# Revit family: VT.VAR10.G.07
name_source: partatom
category: Оборудование
units: mm (PartAtom-declared; Revit-internal decimal feet)

## family parameters
Всегда вертикально = Да
Заголовок OmniClass = Climate Control (HVAC)
На основе рабочей плоскости = Нет
Номер OmniClass = 23.75.00.00
Общий = Нет
При загрузке вырезать с полостями = Нет
Размер круглого соединителя = Использовать диаметр
Тип детали = Нормальный
Точка расчета площади = Нет

## types (1)
- VT.VAR10.G.07
    Article Type = VAR 10
    BIMобъект категории = Другие
    BIMобъект основная категория = Водопровод
    Produced in = Made in Italy
    Product certification = https://www.ivar-group.com
    Revit Version = 2018
    SKU продукта = VARIMIX
    URL = https://valtec.ru
    URL продукта = https://valtec.ru
    Uniclass 2.0 Description = Клапаны
    Uniclass 2015 Name = Системы отопления, охлаждения и охлаждения
    Вес нетто (кг) = 0
    Группа модели = VAR 10
    Группа товаров = VARIMIX
    Изготовитель = IVAR
    Инструкция по установке = https://valtec.ru
    Классификация IFC = Клапан
    Код категории BIMобъекта = Водопроводным-другой
    Код основной категории BIMobject = Водопровод
    Макс рабочая температура (°С) = 120 °C
    Макс рабочее давление (бар) = 10 бары
    Мастерформат 2014 Описание = Отопление, вентиляция и кондиционирование воздуха (HVAC)
    Материал = Латунь - CW617N
    Материал основной = Латунь
    Номинальная высота = 0 мм
    Номинальная ширина = 0 мм
    Общий поток подачи гидравлики = 0.0 л/с
    Описание = Высокотемпературный комплект прямого потока для системы VARIMIX
    Описание NBS = Клапан
    Описание OmniClass = HVAC Специальные продукты и оборудование
    Описание Конфигурации = Высокотемпературный комплект прямого потока для системы VARIMIX.
    Описание статьи = Высокотемпературный комплект прямого потока для системы VARIMIX
    Пенополистрирольная теплоизоляция = Нет
    Полный гидравлический возвратный поток = 0.0 л/с
    Практическое руководство по использованию семьи = - Вы можете выбрать один из трех вариантов о типе насосов. Отметьте эту опцию в параметрах «без насоса» или «электронный насос с переменной скоростью» или «стандартный трехскоростной насос» в свойствах модели.
    Размер соединения = G 1"1/4 M
    Размеры соединения насоса = G 1"1/2 M
    Семейство продуктов = Тепловая электростанция
    Страна изготовитель = Italy
    Техническое описание = https://valtec.ru
    нет насоса = Да
